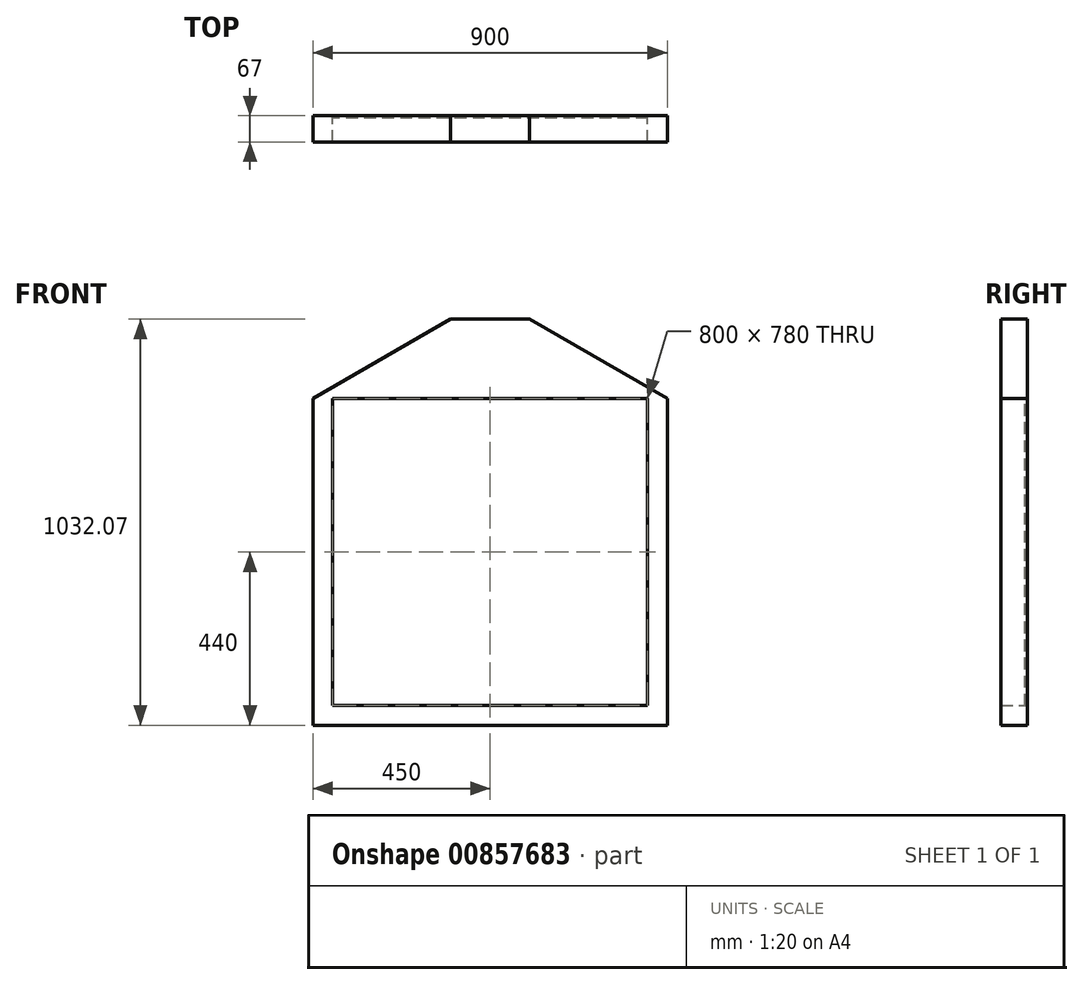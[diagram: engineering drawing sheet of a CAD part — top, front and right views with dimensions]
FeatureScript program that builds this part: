
annotation { "Feature Type Name" : "Feature", "Feature Type Description" : "" }
export const myFeature = defineFeature(function(context is Context, id is Id, definition is map)
    precondition{}
    {
        {
            var Q0;
            Q0=qCreatedBy(makeId("Front.planeOp"),FACE);
            var sketch = newSketch(context, id + "F0", { "sketchPlane" : qUnion([Q0])});
            skLineSegment(sketch, "E0.bottom", {"start": v(450, -415) * mm, "end": v(-450, -415) * mm});
            skLineSegment(sketch, "E0.top", {"start": v(400, 415) * mm, "end": v(-400, 415) * mm});
            skLineSegment(sketch, "E0.left", {"start": v(450, -415) * mm, "end": v(450, 415) * mm});
            skLineSegment(sketch, "E0.right", {"start": v(-450, -415) * mm, "end": v(-450, 415) * mm});
            skPoint(sketch, "E0.middle", {"position": v(0, 0) * mm});
            skLineSegment(sketch, "E1", {"start": v(-450, 415) * mm, "end": v(-100, 617.07) * mm});
            skLineSegment(sketch, "E2", {"start": v(100, 617.07) * mm, "end": v(450, 415) * mm});
            skLineSegment(sketch, "E3.0", {"start": v(-400, -365) * mm, "end": v(-400, 415) * mm});
            skLineSegment(sketch, "E3.1", {"start": v(400, -365) * mm, "end": v(-400, -365) * mm});
            skLineSegment(sketch, "E3.2", {"start": v(400, -365) * mm, "end": v(400, 415) * mm});
            skLineSegment(sketch, "E4", {"start": v(100, 617.07) * mm, "end": v(-100, 617.07) * mm});
            skPoint(sketch, "E5.orphan", {"position": v(0, 674.8) * mm});
            skSolve(sketch);
        }
        {
            var Q0;
            Q0=makeQuery(id+"F0.imprint","IMPRINT",FACE,{"disambiguationData":[TD([[makeQuery(id+"F0.imprint","IMPRINT",EDGE,{"derivedFrom":sQuery(id+"F0.wireOp",EDGE,"E0.bottom")}),-1.0]])]});
            extrude(context, id + "F1", {"entities" : qUnion([Q0]), "depth" : 67 * mm, "offsetDistance" : 25 * mm});
        }
        {
            var Q0;
            Q0=makeQuery(id+"F1.opExtrude","CAP_FACE",FACE,{"disambiguationData":[OSD([sQuery(id+"F0.wireOp",EDGE,"E0.bottom"),sQuery(id+"F0.wireOp",EDGE,"E0.top"),sQuery(id+"F0.wireOp",EDGE,"E0.left"),sQuery(id+"F0.wireOp",EDGE,"E0.right"),sQuery(id+"F0.wireOp",EDGE,"E1"),sQuery(id+"F0.wireOp",EDGE,"E2"),sQuery(id+"F0.wireOp",EDGE,"E3.0"),sQuery(id+"F0.wireOp",EDGE,"E3.1"),sQuery(id+"F0.wireOp",EDGE,"E3.2")])],"isStart":true});
            var sketch = newSketch(context, id + "F2", { "sketchPlane" : qUnion([Q0])});
            skLineSegment(sketch, "E6.bottom", {"start": v(-400, 415) * mm, "end": v(400, 415) * mm});
            skLineSegment(sketch, "E6.top", {"start": v(-400, -365) * mm, "end": v(400, -365) * mm});
            skLineSegment(sketch, "E6.left", {"start": v(-400, 415) * mm, "end": v(-400, -365) * mm});
            skLineSegment(sketch, "E6.right", {"start": v(400, 415) * mm, "end": v(400, -365) * mm});
            skSolve(sketch);
        }
        {
            var Q0;
            Q0=makeQuery(id+"F2.imprint","IMPRINT",FACE,{"disambiguationData":[TD([[makeQuery(id+"F2.imprint","IMPRINT",EDGE,{"derivedFrom":sQuery(id+"F2.wireOp",EDGE,"E6.bottom")}),-1.0]])]});
            extrude(context, id + "F3", {"entities" : qUnion([Q0]), "oppositeDirection" : true, "depth" : 6 * mm, "offsetDistance" : 25 * mm});
        }
    });
